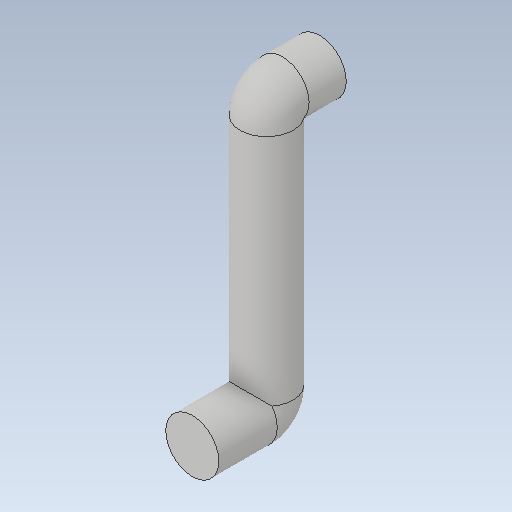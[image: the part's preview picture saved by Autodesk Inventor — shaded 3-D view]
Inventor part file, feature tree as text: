
AUTODESK INVENTOR PART (.ipt)
format: ipt  version: 2020 (Build 240168000, 168)  size: 124,928 bytes
history: native  units: mm
features: sketch x2, plane x1, sweep x1
ambient origin geometry x8: Origin, YZ Plane, XZ Plane, XY Plane, X Axis, Y Axis, Z Axis, Center Point
bodies: Solid1 (feature_tree)
feature tree (4):
  sketch  "3D Sketch6"
  plane  "Work Plane1"
  sweep  "Sweep1"
  sketch  "Sketch7"  dims[d22=50.0mm d23=250.0mm d24=70.0mm d25=50.0mm d26=15.0mm d27=15.0mm d28=0.0mm d29=0.0mm]
